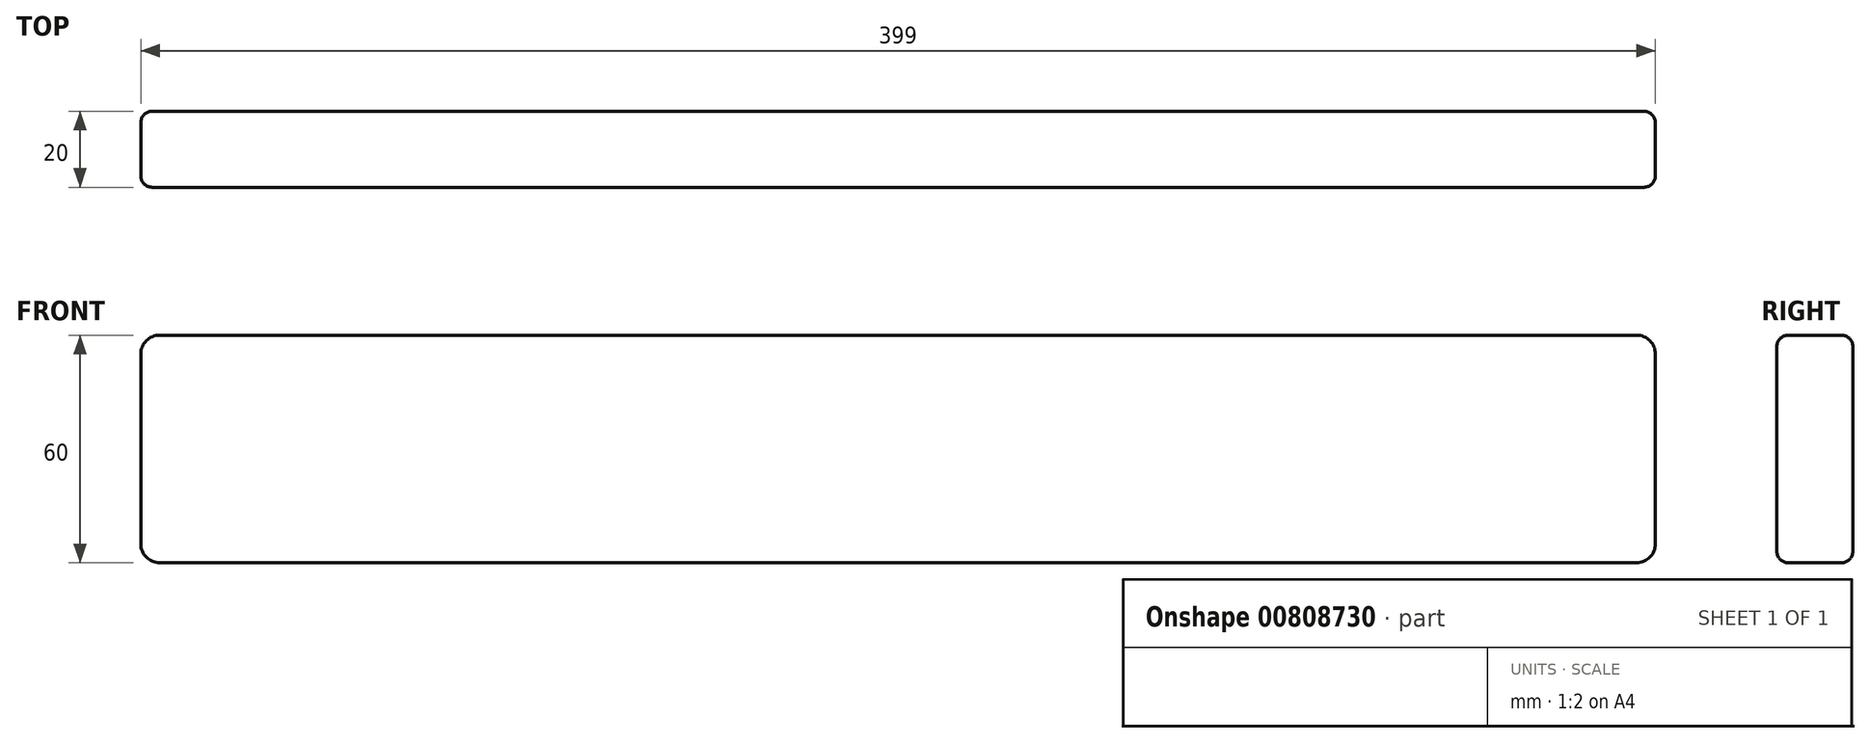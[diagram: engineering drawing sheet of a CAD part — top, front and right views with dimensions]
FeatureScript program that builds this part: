
annotation { "Feature Type Name" : "Feature", "Feature Type Description" : "" }
export const myFeature = defineFeature(function(context is Context, id is Id, definition is map)
    precondition{}
    {
        {
            var Q0;
            Q0=qCreatedBy(makeId("Front.planeOp"),FACE);
            var sketch = newSketch(context, id + "F0", { "sketchPlane" : qUnion([Q0])});
            skLineSegment(sketch, "E0.bottom", {"start": v(194.5, -30) * mm, "end": v(-194.5, -30) * mm});
            skLineSegment(sketch, "E0.top", {"start": v(194.5, 30) * mm, "end": v(-194.5, 30) * mm});
            skLineSegment(sketch, "E0.left", {"start": v(199.5, -25) * mm, "end": v(199.5, 25) * mm});
            skLineSegment(sketch, "E0.right", {"start": v(-199.5, -25) * mm, "end": v(-199.5, 25) * mm});
            skPoint(sketch, "E0.middle", {"position": v(0, 0) * mm});
            skPoint(sketch, "E1.visualSharp", {"position": v(-199.5, 30) * mm});
            skArc(sketch, "E1.filletArc", {"start": v(-194.5, 30) * mm, "mid": v(-198.04, 28.54) * mm, "end": v(-199.5, 25) * mm});
            skPoint(sketch, "E2.visualSharp", {"position": v(-199.5, -30) * mm});
            skArc(sketch, "E2.filletArc", {"start": v(-199.5, -25) * mm, "mid": v(-198.04, -28.54) * mm, "end": v(-194.5, -30) * mm});
            skPoint(sketch, "E3.visualSharp", {"position": v(199.5, -30) * mm});
            skArc(sketch, "E3.filletArc", {"start": v(194.5, -30) * mm, "mid": v(198.04, -28.54) * mm, "end": v(199.5, -25) * mm});
            skPoint(sketch, "E4.visualSharp", {"position": v(199.5, 30) * mm});
            skArc(sketch, "E4.filletArc", {"start": v(199.5, 25) * mm, "mid": v(198.04, 28.54) * mm, "end": v(194.5, 30) * mm});
            skSolve(sketch);
        }
        {
            var Q0;
            Q0=makeQuery(id+"F0.imprint","IMPRINT",FACE,{"disambiguationData":[TD([[makeQuery(id+"F0.imprint","IMPRINT",EDGE,{"derivedFrom":sQuery(id+"F0.wireOp",EDGE,"E0.bottom")}),-1.0]])]});
            extrude(context, id + "F1", {"entities" : qUnion([Q0]), "depth" : 20 * mm, "offsetDistance" : 25 * mm});
        }
        {
            var Q0;
            Q0=makeQuery(id+"F1.opExtrude","CAP_FACE",FACE,{"disambiguationData":[OSD([sQuery(id+"F0.wireOp",EDGE,"E0.bottom"),sQuery(id+"F0.wireOp",EDGE,"E0.top"),sQuery(id+"F0.wireOp",EDGE,"E0.left"),sQuery(id+"F0.wireOp",EDGE,"E0.right"),sQuery(id+"F0.wireOp",EDGE,"E1.filletArc"),sQuery(id+"F0.wireOp",EDGE,"E2.filletArc"),sQuery(id+"F0.wireOp",EDGE,"E3.filletArc"),sQuery(id+"F0.wireOp",EDGE,"E4.filletArc")])],"isStart":false});
            var Q1;
            Q1=makeQuery(id+"F1.opExtrude","CAP_FACE",FACE,{"disambiguationData":[OSD([sQuery(id+"F0.wireOp",EDGE,"E0.bottom"),sQuery(id+"F0.wireOp",EDGE,"E0.top"),sQuery(id+"F0.wireOp",EDGE,"E0.left"),sQuery(id+"F0.wireOp",EDGE,"E0.right"),sQuery(id+"F0.wireOp",EDGE,"E1.filletArc"),sQuery(id+"F0.wireOp",EDGE,"E2.filletArc"),sQuery(id+"F0.wireOp",EDGE,"E3.filletArc"),sQuery(id+"F0.wireOp",EDGE,"E4.filletArc")])],"isStart":true});
            fillet(context, id + "F2", {"entities" : qUnion([Q0, Q1]), "radius" : 3 * mm, "tangentPropagation" : true, "allowEdgeOverflow" : false});
        }
        {
            var Q0;
            Q0=makeQuery(id+"F1.opExtrude","SWEPT_FACE",FACE,{"disambiguationData":[OSD([sQuery(id+"F0.wireOp",EDGE,"E0.left")])]});
            var sketch = newSketch(context, id + "F3", { "sketchPlane" : qUnion([Q0])});
            skPoint(sketch, "E5", {"position": v(-10, 0) * mm});
            skPoint(sketch, "E6.start.orphan", {"position": v(-10, 30) * mm});
            skPoint(sketch, "E7.orphan", {"position": v(-3, 30) * mm});
            skPoint(sketch, "E8.0.start.orphan", {"position": v(-17, 30) * mm});
            skSolve(sketch);
        }
        {
            var Q0;
            Q0=makeQuery(id+"F1.opExtrude","SWEPT_FACE",FACE,{"disambiguationData":[OSD([sQuery(id+"F0.wireOp",EDGE,"E0.right")])]});
            var sketch = newSketch(context, id + "F4", { "sketchPlane" : qUnion([Q0])});
            skPoint(sketch, "E9.0", {"position": v(10, 0) * mm});
            skSolve(sketch);
        }
    });
